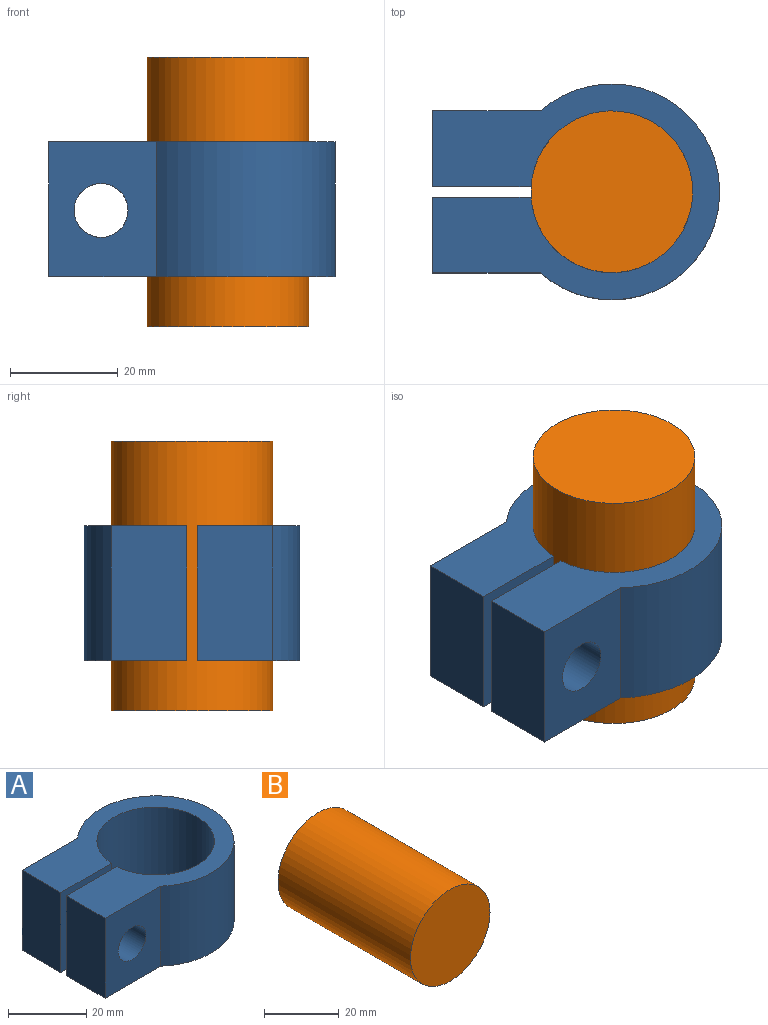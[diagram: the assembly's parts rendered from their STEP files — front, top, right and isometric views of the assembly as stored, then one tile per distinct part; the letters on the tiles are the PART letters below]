
ASSEMBLY  parts=2 mates=1
PART A: 12 faces, bbox 53.2x40x25 mm
  f0: plane 25x18.26mm, normal (0,-1,0), area 378mm2, adj f1,f7,f8,f9,f11
  f1: cylinder r=15mm len=30mm, axis (0,0,-1), area 2306.2mm2, adj f0,f2,f8,f9
  f2: plane 25x18.26mm, normal (0,1,0), area 378mm2, adj f1,f3,f8,f9,f10
  f3: plane 25x14mm, normal (-1,0,0), area 350mm2, adj f2,f4,f8,f9
  f4: plane 25x20mm, normal (0,-1,0), area 421.5mm2, adj f3,f5,f8,f9,f10
  f5: cylinder r=20mm len=40mm, axis (0,0,-1), area 2293.5mm2, adj f4,f6,f8,f9
  f6: plane 25x20mm, normal (0,1,0), area 421.5mm2, adj f5,f7,f8,f9,f11
  f7: plane 25x14mm, normal (-1,0,0), area 350mm2, adj f0,f6,f8,f9
  f8: plane 53.23x40mm, normal (0,0,1), area 972.5mm2, adj f0,f1,f2,f3,f4,f5,f6,f7
  f9: plane 53.23x40mm, normal (0,0,-1), area 972.5mm2, adj f0,f1,f2,f3,f4,f5,f6,f7
  f10: cylinder r=5mm len=14mm, axis (0,1,0), area 439.8mm2, adj f2,f4
  f11: cylinder r=5mm len=14mm, axis (0,1,0), area 439.8mm2, adj f0,f6
PART B: 3 faces, bbox 30x50x30 mm
  f0: cylinder r=15mm len=50mm, axis (0,1,0), area 4712.4mm2, adj f1,f2
  f1: plane 30x30mm, normal (0,-1,0), area 706.9mm2, adj f0
  f2: plane 30x30mm, normal (0,1,0), area 706.9mm2, adj f0
PLACE A t=(16.9,-8.51,0)mm
PLACE B rot(axis=(1,0,0),90deg) t=(-18.56,19.46,40.68)mm
MATE cylindrical B.f0 <-> A.f1  axis (0,0,1) through (16.9,-8.51,40.68)mm
